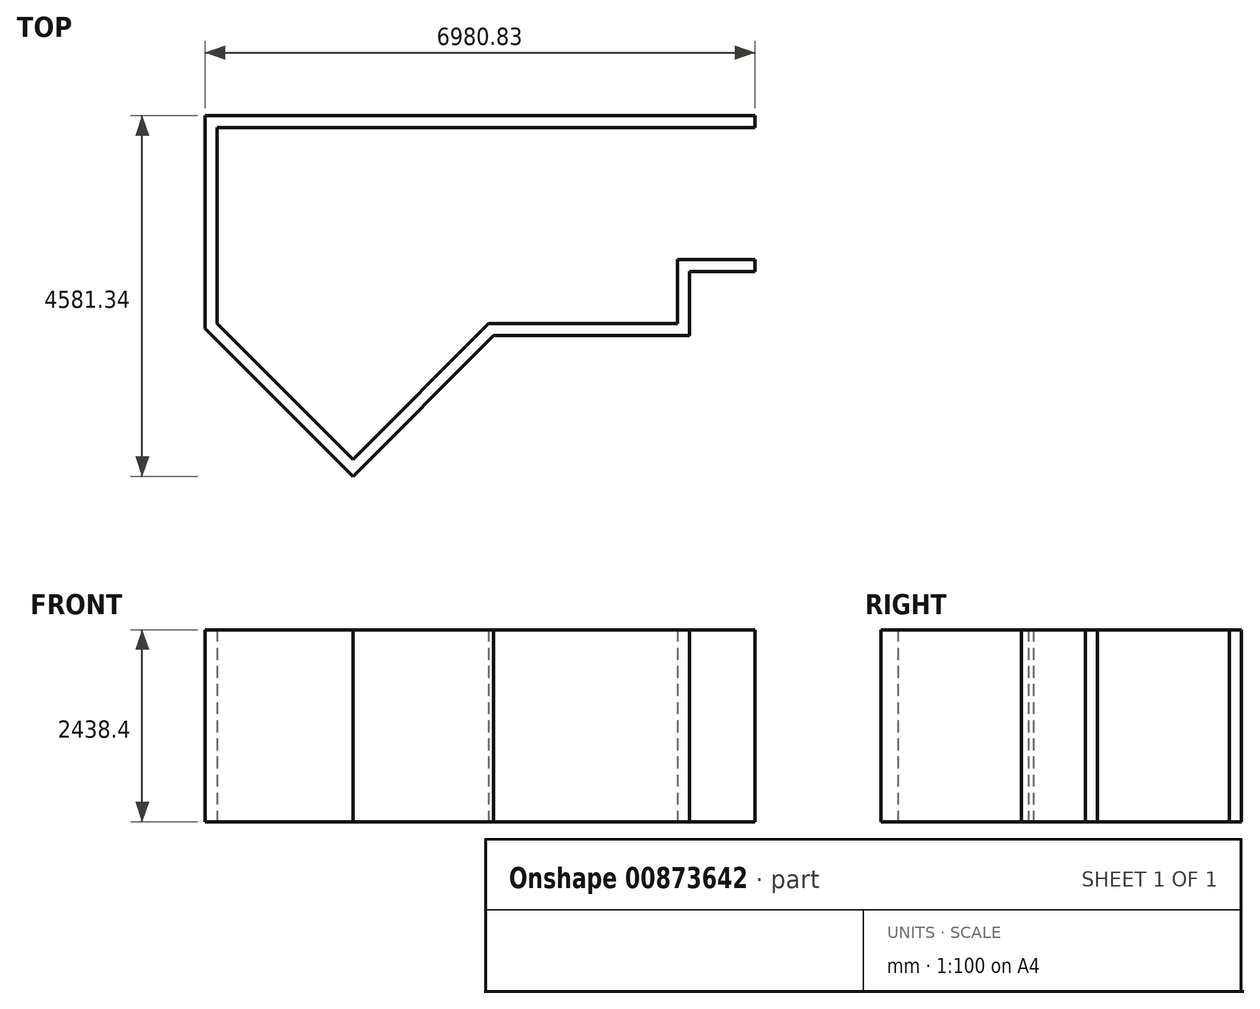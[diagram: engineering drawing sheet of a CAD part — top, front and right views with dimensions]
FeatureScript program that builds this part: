
annotation { "Feature Type Name" : "Feature", "Feature Type Description" : "" }
export const myFeature = defineFeature(function(context is Context, id is Id, definition is map)
    precondition{}
    {
        {
            var Q0;
            Q0=qCreatedBy(makeId("Top.planeOp"),FACE);
            var Q1;
            Q1=qCreatedBy(makeId("Top.planeOp"),FACE);
            var sketch = newSketch(context, id + "F0", { "sketchPlane" : qUnion([Q0, Q1])});
            skLineSegment(sketch, "E0", {"start": v(0, 0) * mm, "end": v(0, 2489.2) * mm});
            skLineSegment(sketch, "E1", {"start": v(0, 0) * mm, "end": v(1724.2, -1724.2) * mm});
            skLineSegment(sketch, "E2", {"start": v(1724.2, -1724.2) * mm, "end": v(3448.42, 0) * mm});
            skLineSegment(sketch, "E3", {"start": v(3448.42, 0) * mm, "end": v(5848.72, 0) * mm});
            skLineSegment(sketch, "E4", {"start": v(5848.72, 0) * mm, "end": v(5848.72, 812.8) * mm});
            skLineSegment(sketch, "E5", {"start": v(5848.72, 812.8) * mm, "end": v(6828.43, 812.8) * mm});
            skLineSegment(sketch, "E6", {"start": v(6828.43, 2489.2) * mm, "end": v(0, 2489.2) * mm});
            skLineSegment(sketch, "E7.0", {"start": v(6828.43, 660.4) * mm, "end": v(6828.43, 812.8) * mm});
            skLineSegment(sketch, "E7.1", {"start": v(6001.12, 660.4) * mm, "end": v(6828.43, 660.4) * mm});
            skLineSegment(sketch, "E7.2", {"start": v(6828.43, 2641.6) * mm, "end": v(-152.4, 2641.6) * mm});
            skLineSegment(sketch, "E7.3", {"start": v(6001.12, -152.4) * mm, "end": v(6001.12, 660.4) * mm});
            skLineSegment(sketch, "E7.4", {"start": v(-152.4, -63.13) * mm, "end": v(-152.4, 2641.6) * mm});
            skLineSegment(sketch, "E7.5", {"start": v(-152.4, -63.13) * mm, "end": v(1724.2, -1939.74) * mm});
            skLineSegment(sketch, "E7.6", {"start": v(1724.2, -1939.74) * mm, "end": v(3511.54, -152.4) * mm});
            skLineSegment(sketch, "E7.7", {"start": v(3511.54, -152.4) * mm, "end": v(6001.12, -152.4) * mm});
            skLineSegment(sketch, "E8.trimOffspring", {"start": v(6828.43, 2489.2) * mm, "end": v(6828.43, 2641.6) * mm});
            skSolve(sketch);
        }
        {
            var Q0;
            Q0 = qSketchRegion(id + "F0", true);
            extrude(context, id + "F1", {"entities" : qUnion([Q0]), "depth" : 2438.4 * mm, "offsetDistance" : 25.4 * mm});
        }
    });
